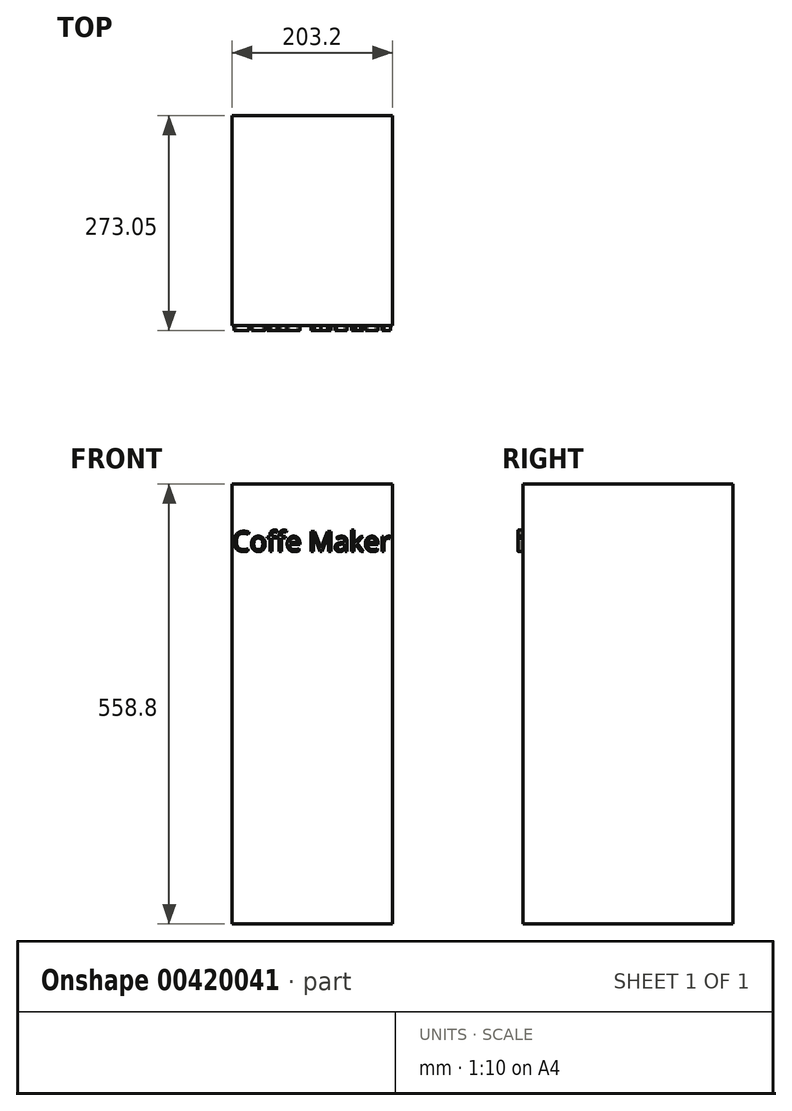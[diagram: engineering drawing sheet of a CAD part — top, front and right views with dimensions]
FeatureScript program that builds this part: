
annotation { "Feature Type Name" : "Feature", "Feature Type Description" : "" }
export const myFeature = defineFeature(function(context is Context, id is Id, definition is map)
    precondition{}
    {
        {
            var Q0;
            Q0=qCreatedBy(makeId("Front.planeOp"),FACE);
            var sketch = newSketch(context, id + "F0", { "sketchPlane" : qUnion([Q0])});
            skLineSegment(sketch, "E0.bottom", {"start": v(0, 0) * mm, "end": v(203.2, 0) * mm});
            skLineSegment(sketch, "E0.top", {"start": v(0, 558.8) * mm, "end": v(203.2, 558.8) * mm});
            skLineSegment(sketch, "E0.left", {"start": v(0, 0) * mm, "end": v(0, 558.8) * mm});
            skLineSegment(sketch, "E0.right", {"start": v(203.2, 0) * mm, "end": v(203.2, 558.8) * mm});
            skSolve(sketch);
        }
        {
            var Q0;
            Q0=makeQuery(id+"F0.imprint","IMPRINT",FACE,{"disambiguationData":[TD([[makeQuery(id+"F0.imprint","IMPRINT",EDGE,{"derivedFrom":sQuery(id+"F0.wireOp",EDGE,"E0.bottom")}),1.0]])]});
            extrude(context, id + "F1", {"entities" : qUnion([Q0]), "depth" : 266.7 * mm});
        }
        {
            var Q0;
            Q0=makeQuery(id+"F1.opExtrude","CAP_FACE",FACE,{"disambiguationData":[OSD([sQuery(id+"F0.wireOp",EDGE,"E0.bottom"),sQuery(id+"F0.wireOp",EDGE,"E0.top"),sQuery(id+"F0.wireOp",EDGE,"E0.left"),sQuery(id+"F0.wireOp",EDGE,"E0.right")])],"isStart":false});
            var sketch = newSketch(context, id + "F2", { "sketchPlane" : qUnion([Q0])});
            skSolve(sketch);
        }
        {
            var Q0;
            Q0=makeQuery(id+"F2.imprint","IMPRINT",FACE,{"disambiguationData":[TD([[makeQuery(id+"F2.imprint","IMPRINT",EDGE,{"derivedFrom":makeQuery(id+"F1.opExtrude","CAP_EDGE",EDGE,{"disambiguationData":[OSD([sQuery(id+"F0.wireOp",EDGE,"E0.bottom")])],"isStart":false})}),1.0]])]});
            var sketch = newSketch(context, id + "F3", { "sketchPlane" : qUnion([Q0])});
            skText(sketch, "E1", { "text": "Coffe Maker", "fontName": "OpenSans-Regular.ttf"});
            const initialGuessF3  = {"E1": [0, 0.47328, 1, 0, 0.0255]};
            skSetInitialGuess(sketch, initialGuessF3);
            skSolve(sketch);
        }
        {
            var Q0;
            Q0 = qSketchRegion(id + "F3", true);
            extrude(context, id + "F4", {"entities" : qUnion([Q0]), "operationType" : NewBodyOperationType.ADD, "depth" : 6.35 * mm});
        }
    });
